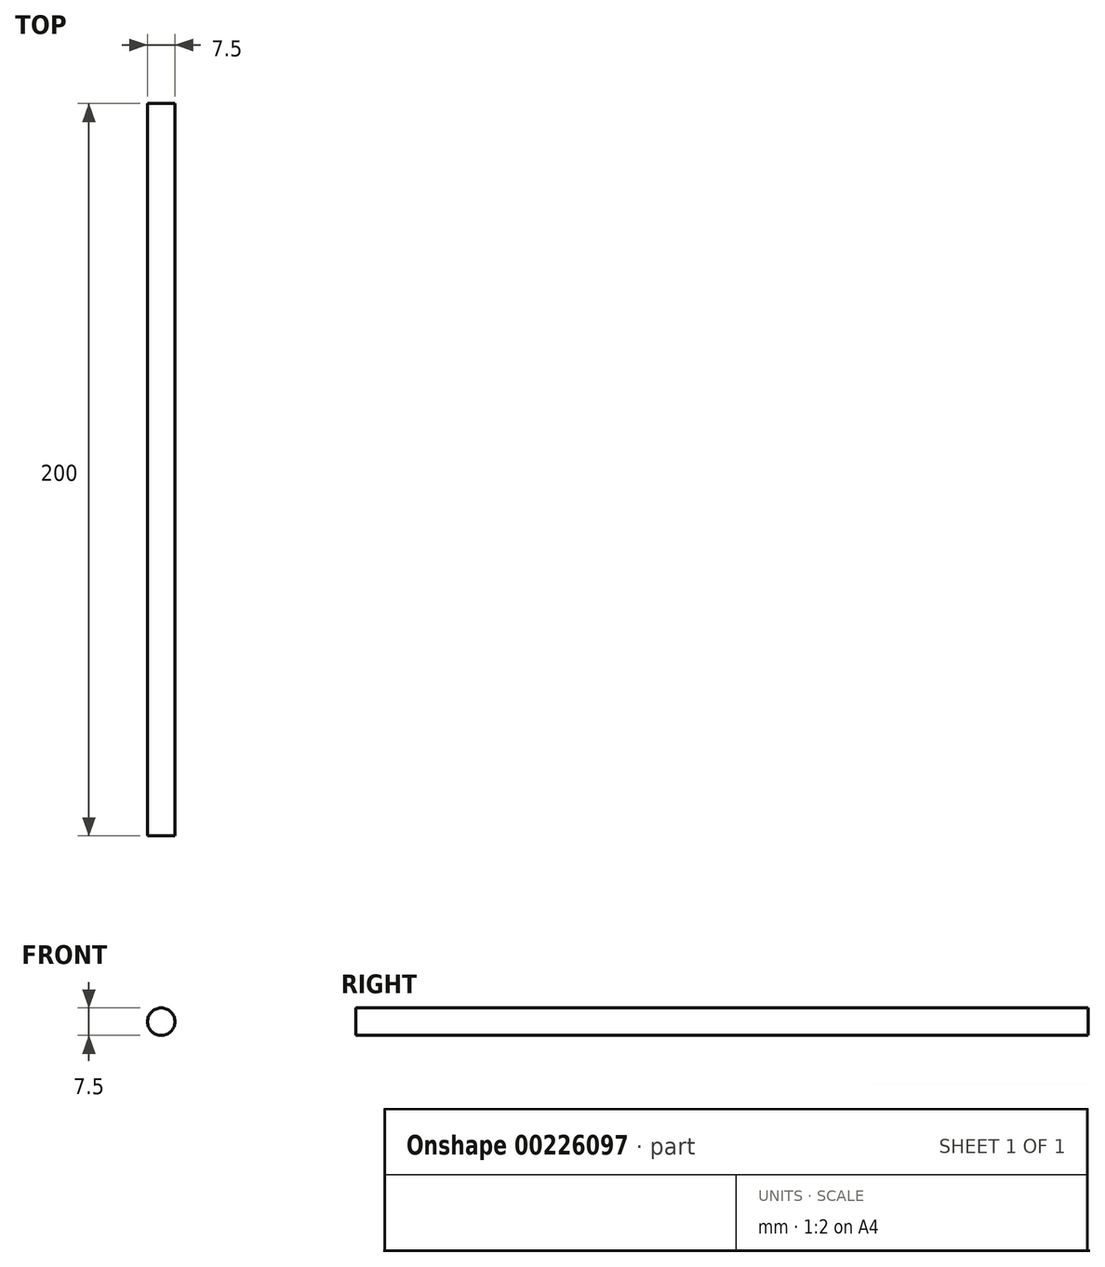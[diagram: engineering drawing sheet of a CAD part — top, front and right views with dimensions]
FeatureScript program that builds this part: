
annotation { "Feature Type Name" : "Feature", "Feature Type Description" : "" }
export const myFeature = defineFeature(function(context is Context, id is Id, definition is map)
    precondition{}
    {
        {
            var Q0;
            Q0=qCreatedBy(makeId("Front.planeOp"),FACE);
            var sketch = newSketch(context, id + "F0", { "sketchPlane" : qUnion([Q0])});
            skCircle(sketch, "E0", {"center": v(0, 0) * mm, "radius": 3.75 * mm});
            skSolve(sketch);
        }
        {
            var Q0;
            Q0 = qSketchRegion(id + "F0", true);
            extrude(context, id + "F1", {"entities" : qUnion([Q0]), "endBound" : BoundingType.SYMMETRIC, "depth" : 200 * mm});
        }
    });
